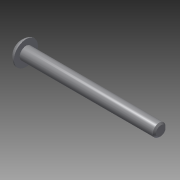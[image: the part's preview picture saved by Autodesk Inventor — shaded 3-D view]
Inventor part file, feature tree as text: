
AUTODESK INVENTOR PART (.ipt)
format: ipt  version: 2015 (Build 190159000, 159)  size: 117,248 bytes
history: native  units: in
note: dims shown in document units (in); Inventor stores cm internally (conversion verified against a paired STEP export)
features: other x3, extrude x1, chamfer x1, imported_body x1, sketch x1
ambient origin geometry x8: Origin, YZ Plane, XZ Plane, XY Plane, X Axis, Y Axis, Z Axis, Center Point
bodies: Body1 (feature_tree)
feature tree (7):
  other  "Bolt 1.75 inch"
  parser-record x1  (decoder bookkeeping rows leaked as tree rows — omitted from the tree; the rows remain in map.json)
  other  "Bolt"
  extrude  "thread length"  Depth=1.75in TaperAngle=0.0deg
  chamfer  "thread chamfer"  Distance=0.02in Angle=45.0deg
  imported_body  "Base1"
  sketch  "Sketch1"  dims[d0=0.164in d1=1.75in d2=0.0in d3=0.02in d4=0.125in d5=45.0deg d7=0.0in d9=0.0in]
